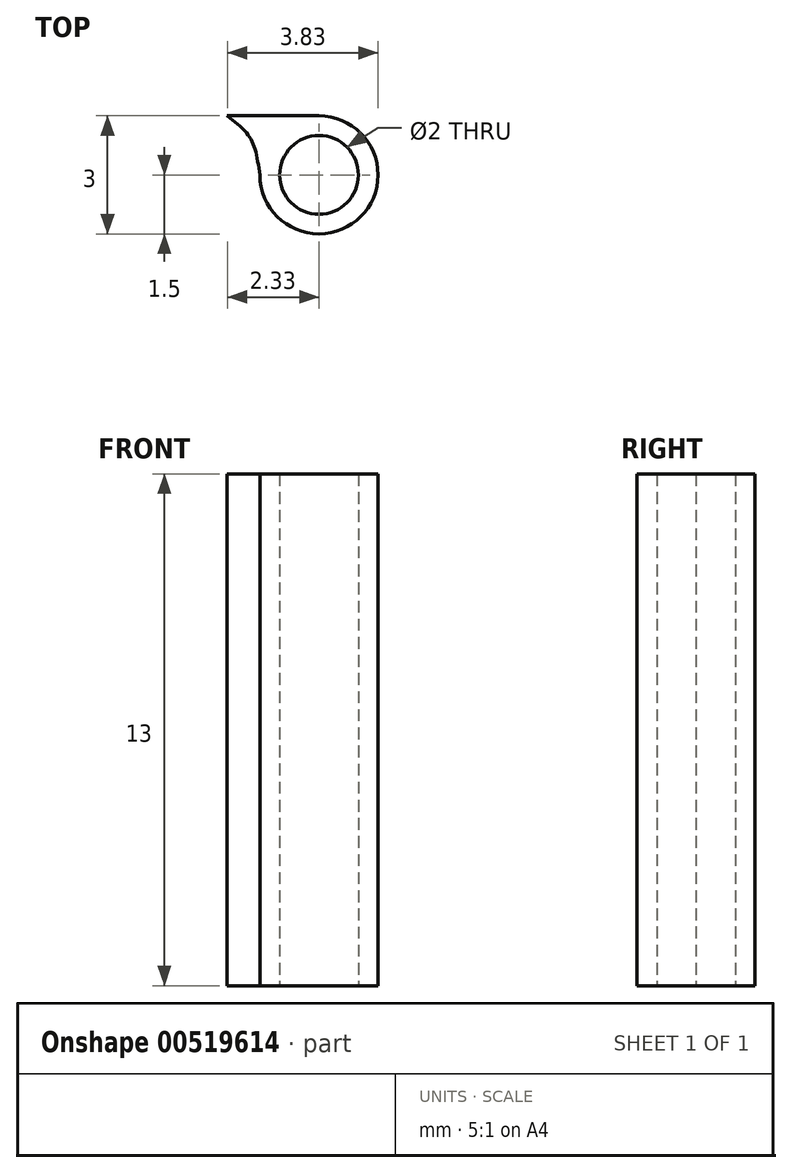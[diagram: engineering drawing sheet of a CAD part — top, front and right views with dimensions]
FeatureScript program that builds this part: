
annotation { "Feature Type Name" : "Feature", "Feature Type Description" : "" }
export const myFeature = defineFeature(function(context is Context, id is Id, definition is map)
    precondition{}
    {
        {
            var Q0;
            Q0=qCreatedBy(makeId("Top.planeOp"),FACE);
            var sketch = newSketch(context, id + "F0", { "sketchPlane" : qUnion([Q0])});
            skCircle(sketch, "E0", {"center": v(0, 0) * mm, "radius": 1 * mm});
            skArc(sketch, "E1", {"start": v(-1.5, 0) * mm, "mid": v(1.06, -1.06) * mm, "end": v(0, 1.5) * mm});
            skLineSegment(sketch, "E2", {"start": v(0, 1.5) * mm, "end": v(-2.33, 1.5) * mm});
            skFitSpline(sketch, "E3", {"points": [v(-2.33, 1.5) * mm, v(-1.84, 1.07) * mm, v(-1.63, 0.67) * mm, v(-1.5, 0) * mm], "startDerivative": vector(1.57, -1.23) * mm, "endDerivative": vector(0.3, -2) * mm});
            skSolve(sketch);
        }
        {
            var Q0;
            Q0=qSketchRegion(id+"F0",true);
            extrude(context, id + "F1", {"entities" : qUnion([Q0]), "depth" : 13 * mm, "offsetDistance" : 25 * mm});
        }
    });
